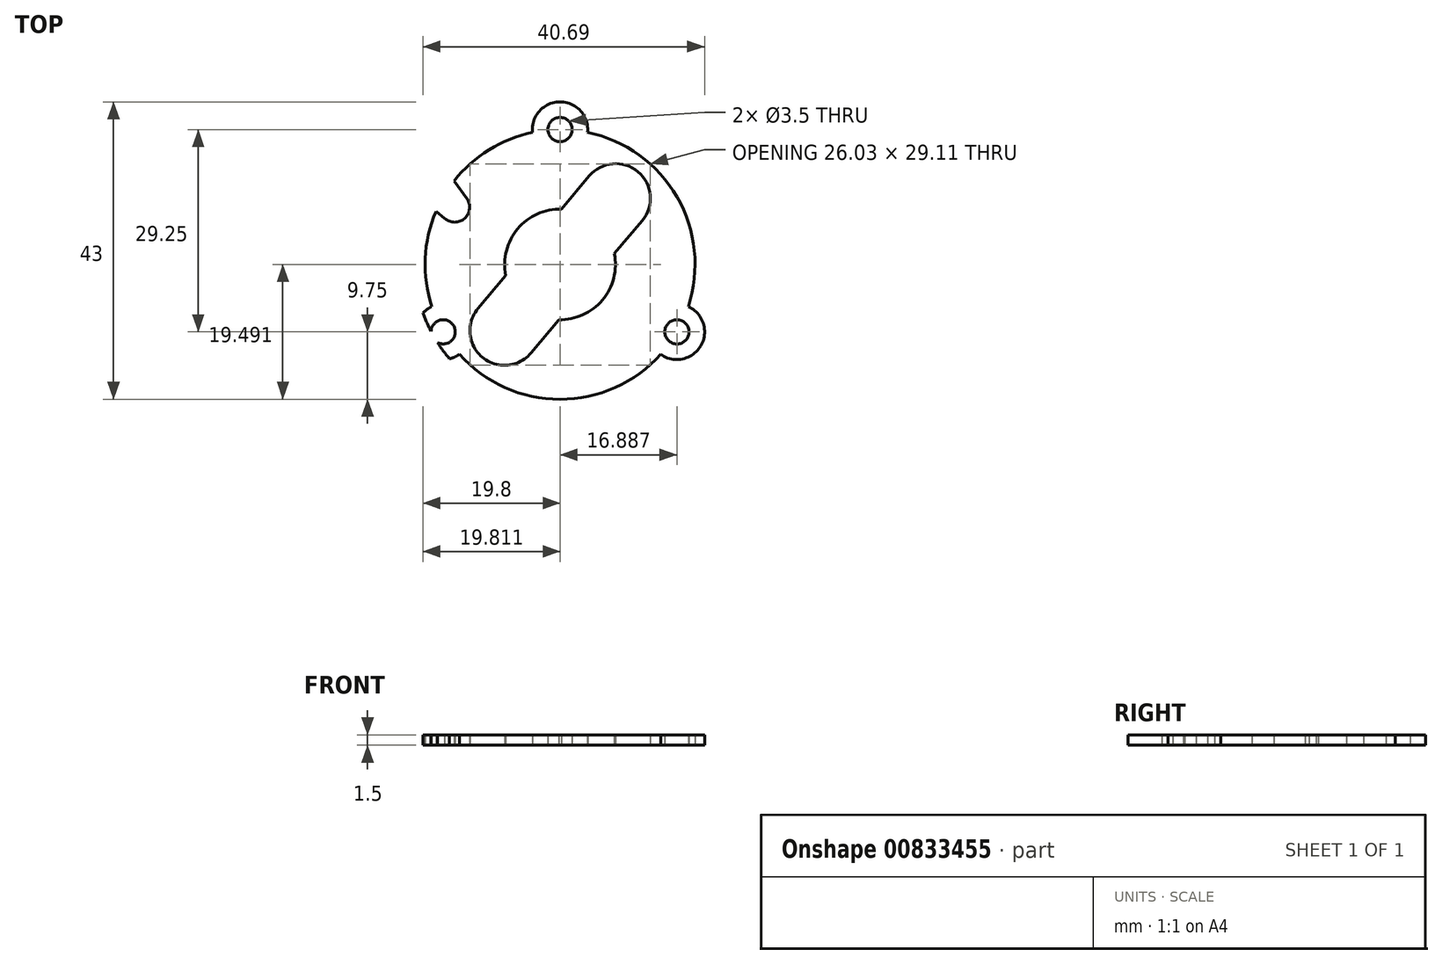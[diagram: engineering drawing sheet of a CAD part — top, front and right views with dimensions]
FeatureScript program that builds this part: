
annotation { "Feature Type Name" : "Feature", "Feature Type Description" : "" }
export const myFeature = defineFeature(function(context is Context, id is Id, definition is map)
    precondition{}
    {
        {
            var Q0;
            Q0=qCreatedBy(makeId("Top.planeOp"),FACE);
            var sketch = newSketch(context, id + "F0", { "sketchPlane" : qUnion([Q0])});
            skArc(sketch, "E0", {"start": v(-17.93, 7.68) * mm, "mid": v(16.76, -9.96) * mm, "end": v(-15.3, 12.08) * mm});
            skCircle(sketch, "E1", {"center": v(0, 19.5) * mm, "radius": 1.75 * mm});
            skCircle(sketch, "E2.1.0", {"center": v(-16.89, -9.75) * mm, "radius": 1.75 * mm});
            skCircle(sketch, "E2.2.0", {"center": v(16.89, -9.75) * mm, "radius": 1.75 * mm});
            skCircle(sketch, "E3", {"center": v(0, 19.5) * mm, "radius": 4 * mm});
            skCircle(sketch, "E4", {"center": v(16.89, -9.75) * mm, "radius": 4 * mm});
            skArc(sketch, "E5", {"start": v(-13.1, -8.47) * mm, "mid": v(-20.88, -9.9) * mm, "end": v(-13.02, -10.76) * mm});
            skLineSegment(sketch, "E6", {"start": v(0, 19.5) * mm, "end": v(4, 19.5) * mm});
            skLineSegment(sketch, "E7", {"start": v(0, 19.5) * mm, "end": v(-4, 19.5) * mm});
            skArc(sketch, "E8", {"start": v(-19.14, 8.65) * mm, "mid": v(17.83, -11.09) * mm, "end": v(-16.22, 13.34) * mm});
            skArc(sketch, "E9", {"start": v(-16.68, 6.68) * mm, "mid": v(-13.79, 6.65) * mm, "end": v(-13.47, 9.52) * mm});
            skLineSegment(sketch, "E10", {"start": v(-16.68, 6.68) * mm, "end": v(-19.14, 8.65) * mm});
            skLineSegment(sketch, "E11", {"start": v(-16.22, 13.34) * mm, "end": v(-13.47, 9.52) * mm});
            skArc(sketch, "E12", {"start": v(11.87, 6.35) * mm, "mid": v(11.26, 13.4) * mm, "end": v(4.22, 12.78) * mm});
            skArc(sketch, "E13", {"start": v(-0.18, -8) * mm, "mid": v(6.13, -5.14) * mm, "end": v(7.85, 1.56) * mm});
            skLineSegment(sketch, "E14", {"start": v(0.08, -0.07) * mm, "end": v(0, 0) * mm});
            skLineSegment(sketch, "E15", {"start": v(4.22, 12.78) * mm, "end": v(0.2, 8) * mm});
            skLineSegment(sketch, "E16.MirrorCS", {"start": v(11.87, 6.35) * mm, "end": v(7.85, 1.56) * mm});
            skLineSegment(sketch, "E17.MirrorCS", {"start": v(-11.86, -6.37) * mm, "end": v(-7.84, -1.58) * mm});
            skArc(sketch, "E18.MirrorC", {"start": v(-4.2, -12.8) * mm, "mid": v(-11.23, -13.42) * mm, "end": v(-11.86, -6.37) * mm});
            skLineSegment(sketch, "E19.MirrorCS", {"start": v(-4.2, -12.8) * mm, "end": v(-0.18, -8) * mm});
            skPoint(sketch, "E20.orphan", {"position": v(-3.83, 3.21) * mm});
            skLineSegment(sketch, "E21.trimOffspring", {"start": v(3.83, -3.21) * mm, "end": v(3.83, -3.21) * mm});
            skArc(sketch, "E22.trimOffspring", {"start": v(0.2, 8) * mm, "mid": v(-6.13, 5.14) * mm, "end": v(-7.84, -1.58) * mm});
            skSolve(sketch);
        }
        {
            var Q0;
            {var subQ0=sQuery(id+"F0.wireOp",EDGE,"E1");var subQ1=sQuery(id+"F0.wireOp",EDGE,"E0");var subQ2=makeQuery(id+"F0.imprint","INTERSECT",VERTEX,{"disambiguationData":[OD(0.0)],"derivedFrom":[subQ1,subQ0]});Q0=makeQuery(id+"F0.imprint","IMPRINT",FACE,{"disambiguationData":[TD([[makeQuery(id+"F0.imprint","IMPRINT",EDGE,{"disambiguationData":[TD([[subQ2,1.0]])],"derivedFrom":subQ1}),1.0]])]});}
            var Q1;
            {var subQ0=sQuery(id+"F0.wireOp",EDGE,"E3");var subQ1=sQuery(id+"F0.wireOp",EDGE,"E0");var subQ2=makeQuery(id+"F0.imprint","INTERSECT",VERTEX,{"disambiguationData":[OD(1.0)],"derivedFrom":[subQ1,subQ0]});Q1=makeQuery(id+"F0.imprint","IMPRINT",FACE,{"disambiguationData":[TD([[makeQuery(id+"F0.imprint","IMPRINT",EDGE,{"disambiguationData":[TD([[subQ2,-1.0]])],"derivedFrom":subQ1}),1.0]])]});}
            var Q2;
            {var subQ0=sQuery(id+"F0.wireOp",EDGE,"E3");var subQ1=sQuery(id+"F0.wireOp",EDGE,"E0");var subQ2=makeQuery(id+"F0.imprint","INTERSECT",VERTEX,{"disambiguationData":[OD(0.0)],"derivedFrom":[subQ1,subQ0]});Q2=makeQuery(id+"F0.imprint","IMPRINT",FACE,{"disambiguationData":[TD([[makeQuery(id+"F0.imprint","IMPRINT",EDGE,{"disambiguationData":[TD([[subQ2,1.0]])],"derivedFrom":subQ1}),1.0]])]});}
            var Q3;
            {var subQ0=sQuery(id+"F0.wireOp",EDGE,"E5");var subQ1=sQuery(id+"F0.wireOp",EDGE,"E0");var subQ2=makeQuery(id+"F0.imprint","INTERSECT",VERTEX,{"disambiguationData":[OD(1.0)],"derivedFrom":[subQ1,subQ0]});Q3=makeQuery(id+"F0.imprint","IMPRINT",FACE,{"disambiguationData":[TD([[makeQuery(id+"F0.imprint","IMPRINT",EDGE,{"disambiguationData":[TD([[subQ2,-1.0]])],"derivedFrom":subQ1}),1.0]])]});}
            var Q4;
            {var subQ1=sQuery(id+"F0.wireOp",EDGE,"E0");var subQ4=sQuery(id+"F0.wireOp",EDGE,"E4");var subQ7=makeQuery(id+"F0.imprint","INTERSECT",VERTEX,{"disambiguationData":[OD(0.0)],"derivedFrom":[subQ1,subQ4]});Q4=makeQuery(id+"F0.imprint","IMPRINT",FACE,{"disambiguationData":[TD([[makeQuery(id+"F0.imprint","IMPRINT",EDGE,{"disambiguationData":[TD([[subQ7,-1.0]])],"derivedFrom":subQ1}),1.0]])]});}
            var Q5;
            {var subQ0=sQuery(id+"F0.wireOp",EDGE,"E5");var subQ1=sQuery(id+"F0.wireOp",EDGE,"E0");var subQ2=makeQuery(id+"F0.imprint","INTERSECT",VERTEX,{"disambiguationData":[OD(0.0)],"derivedFrom":[subQ1,subQ0]});Q5=makeQuery(id+"F0.imprint","IMPRINT",FACE,{"disambiguationData":[TD([[makeQuery(id+"F0.imprint","IMPRINT",EDGE,{"disambiguationData":[TD([[subQ2,-1.0]])],"derivedFrom":subQ1}),1.0]])]});}
            var Q6;
            {var subQ0=sQuery(id+"F0.wireOp",EDGE,"E8");var subQ1=sQuery(id+"F0.wireOp",EDGE,"E1");var subQ2=makeQuery(id+"F0.imprint","INTERSECT",VERTEX,{"disambiguationData":[OD(0.0)],"derivedFrom":[subQ1,subQ0]});Q6=makeQuery(id+"F0.imprint","IMPRINT",FACE,{"disambiguationData":[TD([[makeQuery(id+"F0.imprint","IMPRINT",EDGE,{"disambiguationData":[TD([[subQ2,-1.0]])],"derivedFrom":subQ1}),-1.0]])]});}
            var Q7;
            {var subQ0=sQuery(id+"F0.wireOp",EDGE,"E8");var subQ1=sQuery(id+"F0.wireOp",EDGE,"E1");var subQ2=makeQuery(id+"F0.imprint","INTERSECT",VERTEX,{"disambiguationData":[OD(1.0)],"derivedFrom":[subQ1,subQ0]});Q7=makeQuery(id+"F0.imprint","IMPRINT",FACE,{"disambiguationData":[TD([[makeQuery(id+"F0.imprint","IMPRINT",EDGE,{"disambiguationData":[TD([[subQ2,-1.0]])],"derivedFrom":subQ1}),-1.0]])]});}
            var Q8;
            {var subQ0=sQuery(id+"F0.wireOp",EDGE,"E1");var subQ1=sQuery(id+"F0.wireOp",EDGE,"E0");var subQ2=makeQuery(id+"F0.imprint","INTERSECT",VERTEX,{"disambiguationData":[OD(1.0)],"derivedFrom":[subQ1,subQ0]});Q8=makeQuery(id+"F0.imprint","IMPRINT",FACE,{"disambiguationData":[TD([[makeQuery(id+"F0.imprint","IMPRINT",EDGE,{"disambiguationData":[TD([[subQ2,-1.0]])],"derivedFrom":subQ1}),-1.0]])]});}
            var Q9;
            {var subQ0=sQuery(id+"F0.wireOp",EDGE,"E8");var subQ1=sQuery(id+"F0.wireOp",EDGE,"E1");var subQ2=makeQuery(id+"F0.imprint","INTERSECT",VERTEX,{"disambiguationData":[OD(0.0)],"derivedFrom":[subQ1,subQ0]});Q9=makeQuery(id+"F0.imprint","IMPRINT",FACE,{"disambiguationData":[TD([[makeQuery(id+"F0.imprint","IMPRINT",EDGE,{"disambiguationData":[TD([[subQ2,1.0]])],"derivedFrom":subQ1}),-1.0]])]});}
            var Q10;
            {var subQ0=sQuery(id+"F0.wireOp",EDGE,"E1");var subQ1=sQuery(id+"F0.wireOp",EDGE,"E0");var subQ2=makeQuery(id+"F0.imprint","INTERSECT",VERTEX,{"disambiguationData":[OD(0.0)],"derivedFrom":[subQ1,subQ0]});Q10=makeQuery(id+"F0.imprint","IMPRINT",FACE,{"disambiguationData":[TD([[makeQuery(id+"F0.imprint","IMPRINT",EDGE,{"disambiguationData":[TD([[subQ2,1.0]])],"derivedFrom":subQ1}),-1.0]])]});}
            var Q11;
            {var subQ0=sQuery(id+"F0.wireOp",EDGE,"E5");var subQ1=sQuery(id+"F0.wireOp",EDGE,"E0");var subQ2=makeQuery(id+"F0.imprint","INTERSECT",VERTEX,{"disambiguationData":[OD(0.0)],"derivedFrom":[subQ1,subQ0]});Q11=makeQuery(id+"F0.imprint","IMPRINT",FACE,{"disambiguationData":[TD([[makeQuery(id+"F0.imprint","IMPRINT",EDGE,{"disambiguationData":[TD([[subQ2,-1.0]])],"derivedFrom":subQ1}),-1.0]])]});}
            var Q12;
            {var subQ2=sQuery(id+"F0.wireOp",EDGE,"E8");var subQ4=sQuery(id+"F0.wireOp",EDGE,"E2.1.0");var subQ7=makeQuery(id+"F0.imprint","INTERSECT",VERTEX,{"disambiguationData":[OD(0.0)],"derivedFrom":[subQ4,subQ2]});Q12=makeQuery(id+"F0.imprint","IMPRINT",FACE,{"disambiguationData":[TD([[makeQuery(id+"F0.imprint","IMPRINT",EDGE,{"disambiguationData":[TD([[subQ7,1.0]])],"derivedFrom":subQ4}),-1.0]])]});}
            var Q13;
            {var subQ0=sQuery(id+"F0.wireOp",EDGE,"E2.1.0");var subQ1=sQuery(id+"F0.wireOp",EDGE,"E0");var subQ2=makeQuery(id+"F0.imprint","INTERSECT",VERTEX,{"disambiguationData":[OD(1.0)],"derivedFrom":[subQ1,subQ0]});Q13=makeQuery(id+"F0.imprint","IMPRINT",FACE,{"disambiguationData":[TD([[makeQuery(id+"F0.imprint","IMPRINT",EDGE,{"disambiguationData":[TD([[subQ2,-1.0]])],"derivedFrom":subQ1}),-1.0]])]});}
            var Q14;
            {var subQ0=sQuery(id+"F0.wireOp",EDGE,"E2.2.0");var subQ1=sQuery(id+"F0.wireOp",EDGE,"E0");var subQ2=makeQuery(id+"F0.imprint","INTERSECT",VERTEX,{"disambiguationData":[OD(1.0)],"derivedFrom":[subQ1,subQ0]});Q14=makeQuery(id+"F0.imprint","IMPRINT",FACE,{"disambiguationData":[TD([[makeQuery(id+"F0.imprint","IMPRINT",EDGE,{"disambiguationData":[TD([[subQ2,-1.0]])],"derivedFrom":subQ1}),-1.0]])]});}
            var Q15;
            {var subQ0=sQuery(id+"F0.wireOp",EDGE,"E4");var subQ1=sQuery(id+"F0.wireOp",EDGE,"E0");var subQ2=makeQuery(id+"F0.imprint","INTERSECT",VERTEX,{"disambiguationData":[OD(0.0)],"derivedFrom":[subQ1,subQ0]});Q15=makeQuery(id+"F0.imprint","IMPRINT",FACE,{"disambiguationData":[TD([[makeQuery(id+"F0.imprint","IMPRINT",EDGE,{"disambiguationData":[TD([[subQ2,-1.0]])],"derivedFrom":subQ1}),-1.0]])]});}
            var Q16;
            {var subQ0=sQuery(id+"F0.wireOp",EDGE,"E8");var subQ1=sQuery(id+"F0.wireOp",EDGE,"E2.2.0");var subQ7=makeQuery(id+"F0.imprint","INTERSECT",VERTEX,{"disambiguationData":[OD(0.0)],"derivedFrom":[subQ1,subQ0]});Q16=makeQuery(id+"F0.imprint","IMPRINT",FACE,{"disambiguationData":[TD([[makeQuery(id+"F0.imprint","IMPRINT",EDGE,{"disambiguationData":[TD([[subQ7,1.0]])],"derivedFrom":subQ1}),-1.0]])]});}
            var Q17;
            Q17=makeQuery(id+"F0.imprint","IMPRINT",FACE,{"disambiguationData":[TD([[makeQuery(id+"F0.imprint","IMPRINT",EDGE,{"derivedFrom":sQuery(id+"F0.wireOp",EDGE,"iPhpahmk-HFUo-YhZK-kXP3-ykdmb8G6nFP8")}),-1.0]])]});
            var Q18;
            {var subQ0=sQuery(id+"F0.wireOp",EDGE,"E10");var subQ1=sQuery(id+"F0.wireOp",EDGE,"E0");var subQ2=makeQuery(id+"F0.imprint","INTERSECT",VERTEX,{"derivedFrom":[subQ1,subQ0]});Q18=makeQuery(id+"F0.imprint","IMPRINT",FACE,{"disambiguationData":[TD([[makeQuery(id+"F0.imprint","IMPRINT",EDGE,{"disambiguationData":[TD([[subQ2,-1.0]])],"derivedFrom":subQ1}),1.0]])]});}
            var Q19;
            {var subQ8=sQuery(id+"F0.wireOp",EDGE,"8029dc1c-2227-40a2-877d-2100bbc4be03.trimOffspring");Q19=makeQuery(id+"F0.imprint","IMPRINT",FACE,{"disambiguationData":[TD([[makeQuery(id+"F0.imprint","IMPRINT",EDGE,{"derivedFrom":subQ8}),-1.0]])]});}
            var Q20;
            {var subQ3=sQuery(id+"F0.wireOp",EDGE,"9R65Fwl2-WtWi-83sK-teg3-xmTiWujxEo6U");Q20=makeQuery(id+"F0.imprint","IMPRINT",FACE,{"disambiguationData":[TD([[makeQuery(id+"F0.imprint","IMPRINT",EDGE,{"derivedFrom":subQ3}),-1.0]])]});}
            var Q21;
            {var subQ0=sQuery(id+"F0.wireOp",EDGE,"bQodG5X8-lWhQ-dT0N-S89c-RggMaI9AAa75");var subQ1=sQuery(id+"F0.wireOp",EDGE,"E5");var subQ2=makeQuery(id+"F0.imprint","INTERSECT",VERTEX,{"disambiguationData":[OD(0.0)],"derivedFrom":[subQ1,subQ0]});Q21=makeQuery(id+"F0.imprint","IMPRINT",FACE,{"disambiguationData":[TD([[makeQuery(id+"F0.imprint","IMPRINT",EDGE,{"disambiguationData":[TD([[subQ2,-1.0]])],"derivedFrom":subQ1}),-1.0]])]});}
            extrude(context, id + "F1", {"entities" : qUnion([Q0, Q1, Q2, Q3, Q4, Q5, Q6, Q7, Q8, Q9, Q10, Q11, Q12, Q13, Q14, Q15, Q16, Q17, Q18, Q19, Q20, Q21]), "depth" : 1.5 * mm, "offsetDistance" : 25 * mm});
        }
    });
